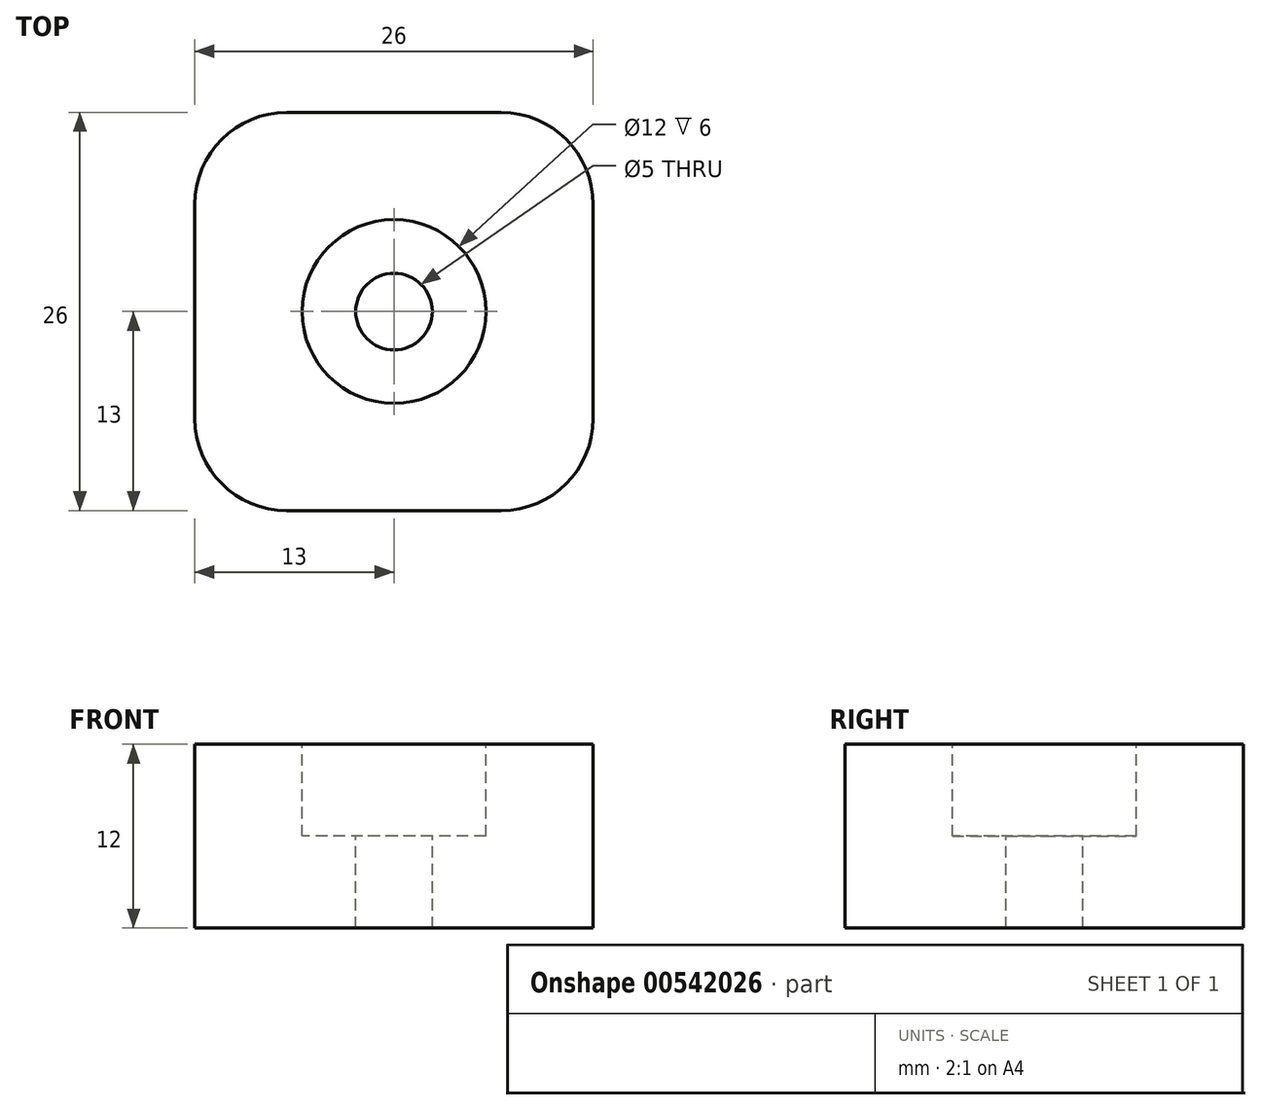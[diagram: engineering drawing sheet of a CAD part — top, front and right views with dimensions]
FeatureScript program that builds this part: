
annotation { "Feature Type Name" : "Feature", "Feature Type Description" : "" }
export const myFeature = defineFeature(function(context is Context, id is Id, definition is map)
    precondition{}
    {
        {
            var Q0;
            Q0=qCreatedBy(makeId("Top.planeOp"),FACE);
            var sketch = newSketch(context, id + "F0", { "sketchPlane" : qUnion([Q0])});
            skLineSegment(sketch, "E0.bottom", {"start": v(7, -13) * mm, "end": v(-7, -13) * mm});
            skLineSegment(sketch, "E0.top", {"start": v(7, 13) * mm, "end": v(-7, 13) * mm});
            skLineSegment(sketch, "E0.left", {"start": v(13, -7) * mm, "end": v(13, 7) * mm});
            skLineSegment(sketch, "E0.right", {"start": v(-13, -7) * mm, "end": v(-13, 7) * mm});
            skPoint(sketch, "E0.middle", {"position": v(0, 0) * mm});
            skPoint(sketch, "E1.visualSharp", {"position": v(-13, 13) * mm});
            skArc(sketch, "E1.filletArc", {"start": v(-7, 13) * mm, "mid": v(-11.24, 11.24) * mm, "end": v(-13, 7) * mm});
            skPoint(sketch, "E2.visualSharp", {"position": v(-13, -13) * mm});
            skArc(sketch, "E2.filletArc", {"start": v(-13, -7) * mm, "mid": v(-11.24, -11.24) * mm, "end": v(-7, -13) * mm});
            skPoint(sketch, "E3.visualSharp", {"position": v(13, 13) * mm});
            skArc(sketch, "E3.filletArc", {"start": v(13, 7) * mm, "mid": v(11.24, 11.24) * mm, "end": v(7, 13) * mm});
            skPoint(sketch, "E4.visualSharp", {"position": v(13, -13) * mm});
            skArc(sketch, "E4.filletArc", {"start": v(7, -13) * mm, "mid": v(11.24, -11.24) * mm, "end": v(13, -7) * mm});
            skSolve(sketch);
        }
        {
            var Q0;
            Q0=qSketchRegion(id+"F0",true);
            extrude(context, id + "F1", {"entities" : qUnion([Q0]), "depth" : 12 * mm});
        }
        {
            var Q0;
            Q0=makeQuery(id+"F1.opExtrude","CAP_FACE",FACE,{"disambiguationData":[OSD([sQuery(id+"F0.wireOp",EDGE,"E0.bottom"),sQuery(id+"F0.wireOp",EDGE,"E0.top"),sQuery(id+"F0.wireOp",EDGE,"E0.left"),sQuery(id+"F0.wireOp",EDGE,"E0.right"),sQuery(id+"F0.wireOp",EDGE,"E1.filletArc"),sQuery(id+"F0.wireOp",EDGE,"E2.filletArc"),sQuery(id+"F0.wireOp",EDGE,"E3.filletArc"),sQuery(id+"F0.wireOp",EDGE,"E4.filletArc")])],"isStart":false});
            var sketch = newSketch(context, id + "F2", { "sketchPlane" : qUnion([Q0])});
            skCircle(sketch, "E5", {"center": v(0, 0) * mm, "radius": 6 * mm});
            skSolve(sketch);
        }
        {
            var Q0;
            Q0=qSketchRegion(id+"F2",true);
            extrude(context, id + "F3", {"entities" : qUnion([Q0]), "operationType" : NewBodyOperationType.REMOVE, "oppositeDirection" : true, "depth" : 6 * mm});
        }
        {
            var Q0;
            Q0=makeQuery(id+"F3.boolean.opBoolean","COPY",FACE,{"derivedFrom":makeQuery(id+"F3.opExtrude","CAP_FACE",FACE,{"disambiguationData":[OSD([sQuery(id+"F2.wireOp",EDGE,"E5")])],"isStart":false})});
            var sketch = newSketch(context, id + "F4", { "sketchPlane" : qUnion([Q0])});
            skCircle(sketch, "E6", {"center": v(0, 0) * mm, "radius": 2.5 * mm});
            skSolve(sketch);
        }
        {
            var Q0;
            Q0=qSketchRegion(id+"F4",true);
            extrude(context, id + "F5", {"entities" : qUnion([Q0]), "operationType" : NewBodyOperationType.REMOVE, "oppositeDirection" : true, "depth" : 31.5 * mm});
        }
    });
